# Revit family: 53bde364-bfcd-49a2-ad91-9c4e9cbf3642
name_source: partatom
category: Casework
revit_build: Autodesk Revit 2016 (Build: 20161004_0715(x64)
units: mm (PartAtom-declared; Revit-internal decimal feet)

## family parameters
Cut with Voids When Loaded = No
Host = Face
OmniClass Number = 23.40.35.17.47.14
OmniClass Title = Bathroom Casework
Room Calculation Point = No
Shared = No

## types (1)
- Not a Type, See Type Catalog
    ADA Compliant = No
    Assembly Code = E2010
    Construction Type = Floor Mount
    Date Modified = 5/31/2018
    Default Elevation = 0"
    Depth = 21 7/8"
    Hardware Included = No
    Height = 34 1/2"
    LG = No
    Left_drawer = No
    Manufacturer = KOHLER Co.
    MasterFormat 1995 = 8715
    MasterFormat 2004 = 08.71.73 SLEV
    Material = Solid Wood and Veneers
    Product Documentation Link = http://www.us.kohler.com
    Product Finish = Default
    Product Name = Damask
    Product Page URL = http://www.us.kohler.com
    Right_drawer = No
    TK = No
    Type = 0
    URL = https://www.us.kohler.com
    Width = 30"

## geometry (parser evidence)
native form markers: Sweep x6
no freeform markers — native parametric forms only
